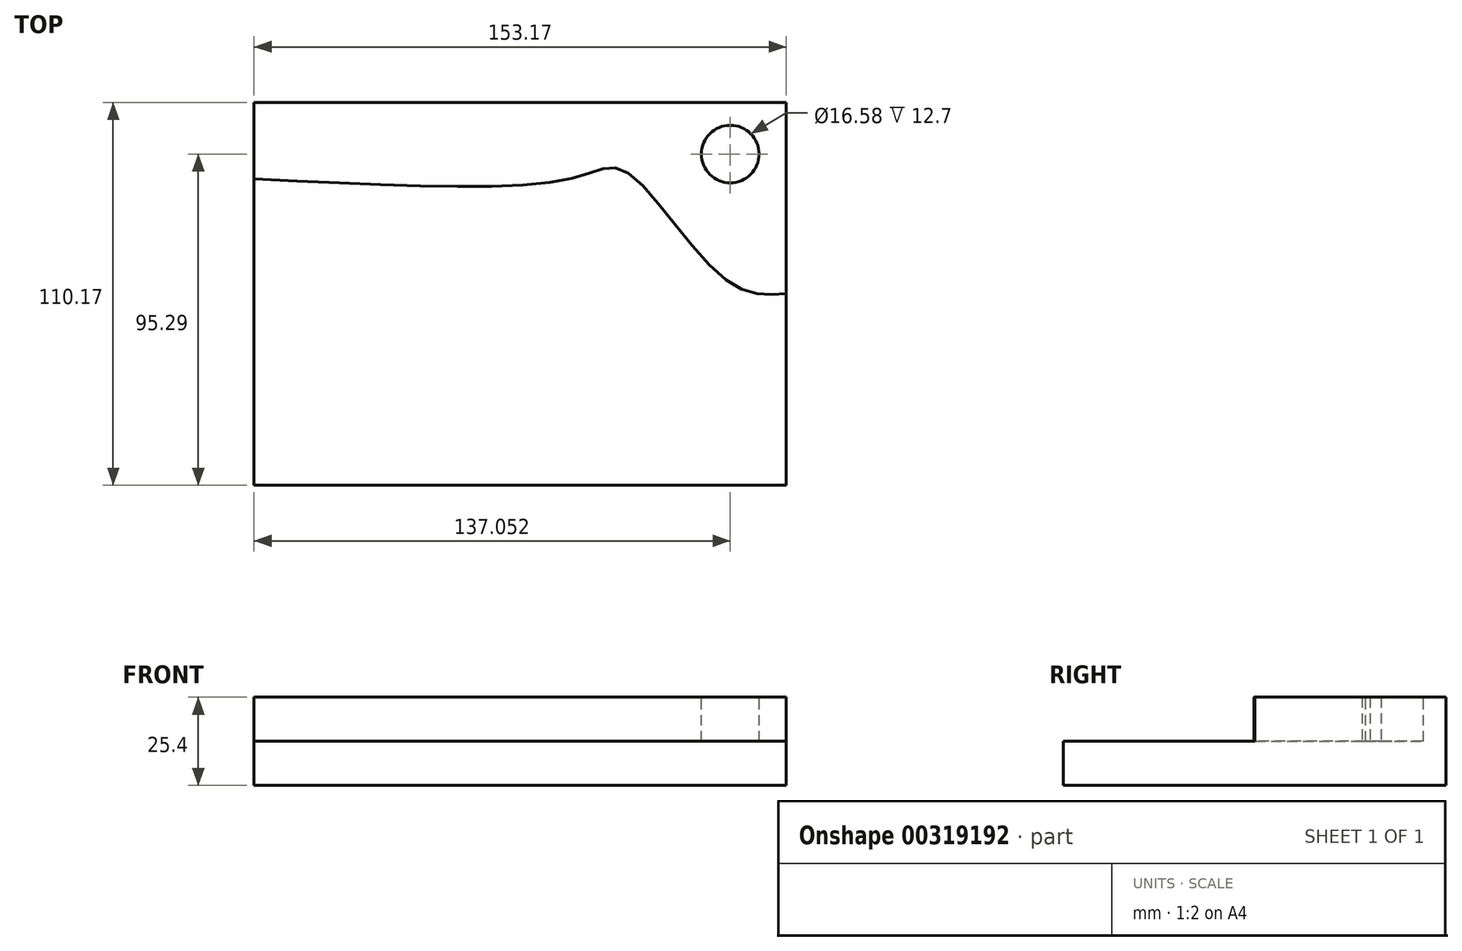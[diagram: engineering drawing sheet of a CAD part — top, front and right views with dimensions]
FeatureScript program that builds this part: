
annotation { "Feature Type Name" : "Feature", "Feature Type Description" : "" }
export const myFeature = defineFeature(function(context is Context, id is Id, definition is map)
    precondition{}
    {
        {
            var Q0;
            Q0=qCreatedBy(makeId("Top.planeOp"),FACE);
            var sketch = newSketch(context, id + "F0", { "sketchPlane" : qUnion([Q0])});
            skLineSegment(sketch, "E0.bottom", {"start": v(12.1, -37.8) * mm, "end": v(-141.08, -37.8) * mm});
            skLineSegment(sketch, "E0.top", {"start": v(12.1, 72.37) * mm, "end": v(-141.08, 72.37) * mm});
            skLineSegment(sketch, "E0.left", {"start": v(12.1, -37.8) * mm, "end": v(12.1, 72.37) * mm});
            skLineSegment(sketch, "E0.right", {"start": v(-141.08, -37.8) * mm, "end": v(-141.08, 72.37) * mm});
            skPoint(sketch, "E0.middle", {"position": v(-64.5, 17.28) * mm});
            skSolve(sketch);
        }
        {
            var Q0;
            Q0 = qSketchRegion(id + "F0", true);
            extrude(context, id + "F1", {"entities" : qUnion([Q0]), "depth" : 12.7 * mm});
        }
        {
            var Q0;
            Q0=makeQuery(id+"F1.opExtrude","CAP_FACE",FACE,{"disambiguationData":[OSD([sQuery(id+"F0.wireOp",EDGE,"E0.bottom"),sQuery(id+"F0.wireOp",EDGE,"E0.top"),sQuery(id+"F0.wireOp",EDGE,"E0.left"),sQuery(id+"F0.wireOp",EDGE,"E0.right")])],"isStart":false});
            var sketch = newSketch(context, id + "F2", { "sketchPlane" : qUnion([Q0])});
            skFitSpline(sketch, "E1", {"points": [v(-141.08, 50.41) * mm, v(-48.93, 50.69) * mm, v(-34.24, 52.6) * mm, v(-5.39, 21.3) * mm, v(12.1, 17.28) * mm], "startDerivative": vector(285.11, -15.26) * mm, "endDerivative": vector(95.92, 6.53) * mm});
            skLineSegment(sketch, "E2", {"start": v(12.1, 17.28) * mm, "end": v(12.1, 72.37) * mm});
            skLineSegment(sketch, "E3", {"start": v(12.1, 72.37) * mm, "end": v(-141.08, 72.37) * mm});
            skLineSegment(sketch, "E4", {"start": v(-141.08, 72.37) * mm, "end": v(-141.08, 50.41) * mm});
            skSolve(sketch);
        }
        {
            var Q0;
            Q0=makeQuery(id+"F2.imprint","IMPRINT",FACE,{"disambiguationData":[TD([[makeQuery(id+"F2.imprint","IMPRINT",EDGE,{"derivedFrom":sQuery(id+"F2.wireOp",EDGE,"E1")}),1.0]])]});
            extrude(context, id + "F3", {"entities" : qUnion([Q0]), "operationType" : NewBodyOperationType.ADD, "depth" : 12.7 * mm});
        }
        {
            var Q0;
            Q0=makeQuery(id+"F3.opExtrude","CAP_FACE",FACE,{"disambiguationData":[OSD([sQuery(id+"F2.wireOp",EDGE,"E1"),sQuery(id+"F2.wireOp",EDGE,"E2"),sQuery(id+"F2.wireOp",EDGE,"E3"),sQuery(id+"F2.wireOp",EDGE,"E4")])],"isStart":false});
            var sketch = newSketch(context, id + "F4", { "sketchPlane" : qUnion([Q0])});
            skCircle(sketch, "E5", {"center": v(-4.03, 57.5) * mm, "radius": 8.3 * mm});
            skSolve(sketch);
        }
        {
            var Q0;
            Q0=makeQuery(id+"F4.imprint","IMPRINT",FACE,{"disambiguationData":[TD([[makeQuery(id+"F4.imprint","IMPRINT",EDGE,{"derivedFrom":sQuery(id+"F4.wireOp",EDGE,"E5")}),1.0]])]});
            extrude(context, id + "F5", {"entities" : qUnion([Q0]), "operationType" : NewBodyOperationType.REMOVE, "oppositeDirection" : true, "depth" : 12.7 * mm});
        }
    });
